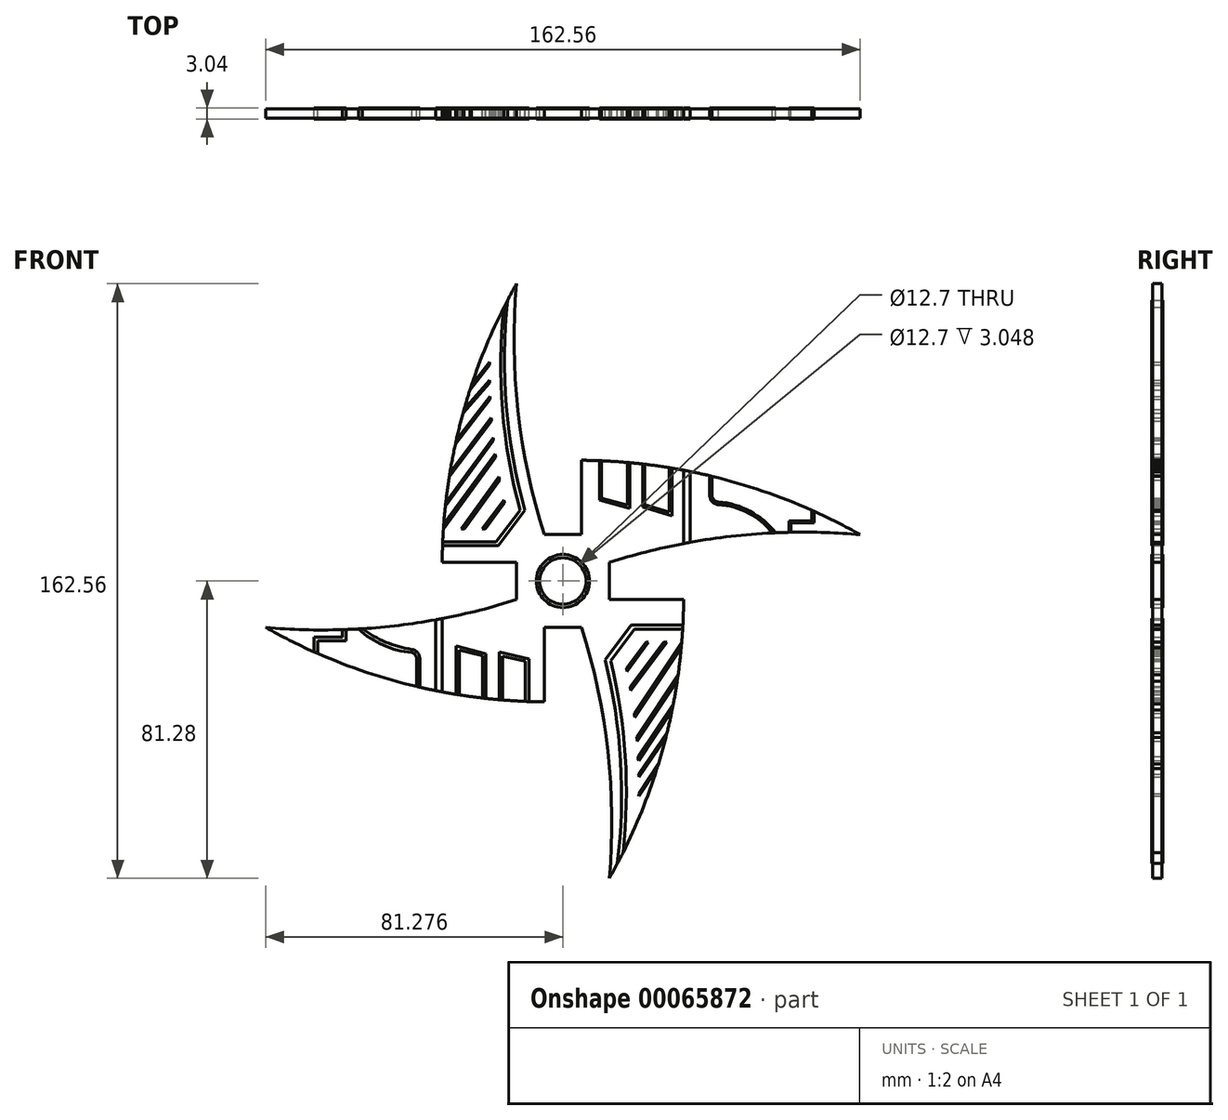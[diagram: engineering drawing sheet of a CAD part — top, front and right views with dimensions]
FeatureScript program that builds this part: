
annotation { "Feature Type Name" : "Feature", "Feature Type Description" : "" }
export const myFeature = defineFeature(function(context is Context, id is Id, definition is map)
    precondition{}
    {
        {
            var Q0;
            Q0=qCreatedBy(makeId("Front.planeOp"),FACE);
            var sketch = newSketch(context, id + "F0", { "sketchPlane" : qUnion([Q0])});
            skCircle(sketch, "E0", {"center": v(-17.65, 17.74) * mm, "radius": 6.35 * mm});
            skLineSegment(sketch, "E1", {"start": v(-22.73, 30.44) * mm, "end": v(-12.57, 30.44) * mm});
            skLineSegment(sketch, "E2", {"start": v(-22.73, 5.04) * mm, "end": v(-12.57, 5.04) * mm});
            skLineSegment(sketch, "E3", {"start": v(-30.35, 22.82) * mm, "end": v(-30.35, 12.66) * mm});
            skLineSegment(sketch, "E4", {"start": v(-4.95, 22.82) * mm, "end": v(-4.95, 12.66) * mm});
            skLineSegment(sketch, "E5", {"start": v(-17.65, 17.74) * mm, "end": v(-17.65, 30.44) * mm, "construction": true});
            skLineSegment(sketch, "E6", {"start": v(-17.65, 17.74) * mm, "end": v(-17.65, 5.04) * mm, "construction": true});
            skLineSegment(sketch, "E7", {"start": v(-17.65, 17.74) * mm, "end": v(-30.35, 17.74) * mm, "construction": true});
            skLineSegment(sketch, "E8", {"start": v(-17.65, 17.74) * mm, "end": v(-4.95, 17.74) * mm, "construction": true});
            skLineSegment(sketch, "E9", {"start": v(-12.57, 30.44) * mm, "end": v(-12.57, 50.76) * mm});
            skLineSegment(sketch, "E10", {"start": v(-4.95, 12.66) * mm, "end": v(15.37, 12.66) * mm});
            skLineSegment(sketch, "E11", {"start": v(-22.73, 5.04) * mm, "end": v(-22.73, -15.28) * mm});
            skLineSegment(sketch, "E12", {"start": v(-30.35, 22.82) * mm, "end": v(-50.67, 22.82) * mm});
            skArc(sketch, "E13", {"start": v(-30.35, 99.02) * mm, "mid": v(-29.96, 64.35) * mm, "end": v(-22.73, 30.44) * mm});
            skArc(sketch, "E14", {"start": v(-30.35, 99.02) * mm, "mid": v(-45.35, 62.21) * mm, "end": v(-50.67, 22.82) * mm});
            skArc(sketch, "E15", {"start": v(63.63, 30.44) * mm, "mid": v(28.96, 30.04) * mm, "end": v(-4.95, 22.82) * mm});
            skArc(sketch, "E16", {"start": v(63.63, 30.44) * mm, "mid": v(26.82, 45.44) * mm, "end": v(-12.57, 50.76) * mm});
            skArc(sketch, "E17", {"start": v(-4.95, -63.54) * mm, "mid": v(-5.35, -28.87) * mm, "end": v(-12.57, 5.04) * mm});
            skArc(sketch, "E18", {"start": v(-4.95, -63.54) * mm, "mid": v(10.05, -26.73) * mm, "end": v(15.37, 12.66) * mm});
            skArc(sketch, "E19", {"start": v(-98.93, 5.04) * mm, "mid": v(-64.26, 5.44) * mm, "end": v(-30.35, 12.66) * mm});
            skArc(sketch, "E20", {"start": v(-98.93, 5.04) * mm, "mid": v(-62.12, -9.96) * mm, "end": v(-22.73, -15.28) * mm});
            skLineSegment(sketch, "E21", {"start": v(-98.93, 5.04) * mm, "end": v(-22.73, 5.04) * mm, "construction": true});
            skLineSegment(sketch, "E22", {"start": v(-30.35, 22.82) * mm, "end": v(-30.35, 99.02) * mm, "construction": true});
            skLineSegment(sketch, "E23", {"start": v(-4.95, -63.54) * mm, "end": v(-4.95, 12.66) * mm, "construction": true});
            skLineSegment(sketch, "E24", {"start": v(-12.57, 30.44) * mm, "end": v(63.63, 30.44) * mm, "construction": true});
            skSolve(sketch);
        }
        {
            var Q0;
            Q0=makeQuery(id+"F0.imprint","IMPRINT",FACE,{"disambiguationData":[TD([[makeQuery(id+"F0.imprint","IMPRINT",EDGE,{"derivedFrom":sQuery(id+"F0.wireOp",EDGE,"E0")}),-1.0]])]});
            extrude(context, id + "F1", {"entities" : qUnion([Q0]), "depth" : 2.54 * mm});
        }
        {
            var Q0;
            Q0=makeQuery(id+"F1.opExtrude","CAP_FACE",FACE,{"disambiguationData":[OSD([sQuery(id+"F0.wireOp",EDGE,"E0"),sQuery(id+"F0.wireOp",EDGE,"E1"),sQuery(id+"F0.wireOp",EDGE,"E2"),sQuery(id+"F0.wireOp",EDGE,"E3"),sQuery(id+"F0.wireOp",EDGE,"E4"),sQuery(id+"F0.wireOp",EDGE,"E9"),sQuery(id+"F0.wireOp",EDGE,"E10"),sQuery(id+"F0.wireOp",EDGE,"E11"),sQuery(id+"F0.wireOp",EDGE,"E12"),sQuery(id+"F0.wireOp",EDGE,"E13"),sQuery(id+"F0.wireOp",EDGE,"E14"),sQuery(id+"F0.wireOp",EDGE,"E15"),sQuery(id+"F0.wireOp",EDGE,"E16"),sQuery(id+"F0.wireOp",EDGE,"E17"),sQuery(id+"F0.wireOp",EDGE,"E18"),sQuery(id+"F0.wireOp",EDGE,"E19"),sQuery(id+"F0.wireOp",EDGE,"E20")])],"isStart":false});
            var sketch = newSketch(context, id + "F2", { "sketchPlane" : qUnion([Q0])});
            skLineSegment(sketch, "E25", {"start": v(-50.53, 28.4) * mm, "end": v(-35.93, 28.4) * mm});
            skArc(sketch, "E26", {"start": v(-33.81, 92.53) * mm, "mid": v(-34.17, 64.62) * mm, "end": v(-29.38, 37.12) * mm});
            skLineSegment(sketch, "E27", {"start": v(-35.93, 28.4) * mm, "end": v(-29.38, 37.12) * mm});
            skArc(sketch, "E28", {"start": v(-37.34, 85.05) * mm, "mid": v(-37.25, 61.92) * mm, "end": v(-33.62, 39.08) * mm});
            skLineSegment(sketch, "E29", {"start": v(-50.33, 32.03) * mm, "end": v(-38.92, 32.03) * mm});
            skLineSegment(sketch, "E30", {"start": v(-38.92, 32.03) * mm, "end": v(-33.62, 39.08) * mm});
            skLineSegment(sketch, "E31", {"start": v(-34.97, 45.3) * mm, "end": v(-44.63, 32.03) * mm});
            skLineSegment(sketch, "E32", {"start": v(-36.06, 51.62) * mm, "end": v(-50.33, 32.03) * mm});
            skLineSegment(sketch, "E33", {"start": v(-36.68, 56.2) * mm, "end": v(-49.8, 38.19) * mm});
            skLineSegment(sketch, "E34", {"start": v(-37.22, 61.53) * mm, "end": v(-48.73, 46.26) * mm});
            skLineSegment(sketch, "E35", {"start": v(-37.6, 67.4) * mm, "end": v(-47.04, 55.25) * mm});
            skLineSegment(sketch, "E36", {"start": v(-37.73, 71.9) * mm, "end": v(-44.98, 63.6) * mm});
            skLineSegment(sketch, "E37", {"start": v(-37.72, 76.84) * mm, "end": v(-43.05, 70.03) * mm});
            skLineSegment(sketch, "E38", {"start": v(-7.06, 50.62) * mm, "end": v(-7.06, 40.35) * mm});
            skLineSegment(sketch, "E39", {"start": v(-7.06, 40.35) * mm, "end": v(0, 38.5) * mm});
            skLineSegment(sketch, "E40", {"start": v(0, 38.5) * mm, "end": v(0, 50.16) * mm});
            skLineSegment(sketch, "E41", {"start": v(4.75, 49.67) * mm, "end": v(4.75, 38.56) * mm});
            skLineSegment(sketch, "E42", {"start": v(4.75, 38.56) * mm, "end": v(11.46, 36.57) * mm});
            skLineSegment(sketch, "E43", {"start": v(11.46, 36.57) * mm, "end": v(11.46, 48.73) * mm});
            skLineSegment(sketch, "E44", {"start": v(15.37, 48.04) * mm, "end": v(15.37, 28) * mm});
            skLineSegment(sketch, "E45", {"start": v(17.18, 28.33) * mm, "end": v(17.18, 47.69) * mm});
            skLineSegment(sketch, "E46", {"start": v(22.5, 46.53) * mm, "end": v(22.5, 41.17) * mm});
            skCircle(sketch, "E47", {"center": v(-17.65, 17.74) * mm, "radius": 7.27 * mm});
            skLineSegment(sketch, "E48", {"start": v(-50.67, 7.49) * mm, "end": v(-50.67, -12.56) * mm});
            skLineSegment(sketch, "E49", {"start": v(-45.94, -13.38) * mm, "end": v(-45.94, -1.07) * mm});
            skLineSegment(sketch, "E50", {"start": v(-45.94, -1.07) * mm, "end": v(-39.58, -2.68) * mm});
            skLineSegment(sketch, "E51", {"start": v(-39.58, -2.68) * mm, "end": v(-39.58, -14.24) * mm});
            skLineSegment(sketch, "E52", {"start": v(-34.2, -14.77) * mm, "end": v(-34.2, -2.78) * mm});
            skLineSegment(sketch, "E53", {"start": v(-34.2, -2.78) * mm, "end": v(-27.89, -4.22) * mm});
            skLineSegment(sketch, "E54", {"start": v(-27.89, -4.22) * mm, "end": v(-27.89, -15.16) * mm});
            skLineSegment(sketch, "E55", {"start": v(-52.49, 7.15) * mm, "end": v(-52.49, -12.2) * mm});
            skLineSegment(sketch, "E56", {"start": v(-56.8, -11.28) * mm, "end": v(-56.8, -3.47) * mm});
            skArc(sketch, "E57", {"start": v(-72.56, 4.71) * mm, "mid": v(-66.1, 1.05) * mm, "end": v(-58.96, -0.96) * mm});
            skPoint(sketch, "E58.visualSharp", {"position": v(-56.8, -1.21) * mm});
            skArc(sketch, "E58.filletArc", {"start": v(-56.8, -3.47) * mm, "mid": v(-57.41, -1.81) * mm, "end": v(-58.96, -0.96) * mm});
            skLineSegment(sketch, "E59", {"start": v(-76.99, 4.49) * mm, "end": v(-76.99, 1.34) * mm});
            skLineSegment(sketch, "E60", {"start": v(-76.99, 1.34) * mm, "end": v(-84.75, 1.34) * mm});
            skLineSegment(sketch, "E61", {"start": v(-84.75, 1.34) * mm, "end": v(-84.75, -2.04) * mm});
            skLineSegment(sketch, "E62", {"start": v(44.22, 31.07) * mm, "end": v(44.22, 34.13) * mm});
            skLineSegment(sketch, "E63", {"start": v(44.22, 34.13) * mm, "end": v(50.44, 34.13) * mm});
            skLineSegment(sketch, "E64", {"start": v(50.44, 34.13) * mm, "end": v(50.44, 37.08) * mm});
            skArc(sketch, "E65", {"start": v(39.59, 30.9) * mm, "mid": v(33.07, 36.35) * mm, "end": v(24.89, 38.64) * mm});
            skPoint(sketch, "E66.visualSharp", {"position": v(22.5, 38.64) * mm});
            skArc(sketch, "E66.filletArc", {"start": v(22.5, 41.17) * mm, "mid": v(23.19, 39.43) * mm, "end": v(24.89, 38.64) * mm});
            skArc(sketch, "E67", {"start": v(-1.2, -56.47) * mm, "mid": v(-0.61, -30.14) * mm, "end": v(-4.62, -4.12) * mm});
            skLineSegment(sketch, "E68", {"start": v(-4.62, -4.12) * mm, "end": v(1.9, 4.56) * mm});
            skLineSegment(sketch, "E69", {"start": v(1.9, 4.56) * mm, "end": v(15.1, 4.56) * mm});
            skLineSegment(sketch, "E70", {"start": v(5.02, 1) * mm, "end": v(14.84, 1) * mm});
            skLineSegment(sketch, "E71", {"start": v(5.02, 1) * mm, "end": v(-0.28, -6.04) * mm});
            skArc(sketch, "E72", {"start": v(2.82, -47.75) * mm, "mid": v(2.72, -26.79) * mm, "end": v(-0.28, -6.04) * mm});
            skLineSegment(sketch, "E73", {"start": v(0.75, -11.2) * mm, "end": v(9.93, 1) * mm});
            skLineSegment(sketch, "E74", {"start": v(1.87, -18.44) * mm, "end": v(14.84, 1) * mm});
            skLineSegment(sketch, "E75", {"start": v(2.57, -24.84) * mm, "end": v(13.85, -7.92) * mm});
            skLineSegment(sketch, "E76", {"start": v(2.94, -30.25) * mm, "end": v(12.53, -15.88) * mm});
            skLineSegment(sketch, "E77", {"start": v(3.12, -40.32) * mm, "end": v(8.46, -32.26) * mm});
            skLineSegment(sketch, "E78", {"start": v(3.11, -35.02) * mm, "end": v(10.82, -23.73) * mm});
            skLineSegment(sketch, "E79", {"start": v(-37.7, 77.6) * mm, "end": v(-42.64, 71.29) * mm});
            skLineSegment(sketch, "E80", {"start": v(-37.74, 72.63) * mm, "end": v(-44.67, 64.68) * mm});
            skLineSegment(sketch, "E81", {"start": v(-37.63, 68.2) * mm, "end": v(-46.78, 56.44) * mm});
            skLineSegment(sketch, "E82", {"start": v(-37.29, 62.36) * mm, "end": v(-48.54, 47.44) * mm});
            skLineSegment(sketch, "E83", {"start": v(-36.76, 56.94) * mm, "end": v(-49.7, 39.19) * mm});
            skLineSegment(sketch, "E84", {"start": v(-36.2, 52.52) * mm, "end": v(-50.25, 33.22) * mm});
            skLineSegment(sketch, "E85", {"start": v(-35.14, 46.2) * mm, "end": v(-45.47, 32.03) * mm});
            skLineSegment(sketch, "E86", {"start": v(-33.8, 39.85) * mm, "end": v(-39.7, 32.03) * mm});
            skLineSegment(sketch, "E87", {"start": v(-50.57, 27.5) * mm, "end": v(-35.27, 27.5) * mm});
            skLineSegment(sketch, "E88", {"start": v(-35.27, 27.5) * mm, "end": v(-28.03, 37.12) * mm});
            skLineSegment(sketch, "E89", {"start": v(-7.65, 50.64) * mm, "end": v(-7.65, 39.9) * mm});
            skLineSegment(sketch, "E90", {"start": v(-7.65, 39.9) * mm, "end": v(0.6, 37.66) * mm});
            skLineSegment(sketch, "E91", {"start": v(0.6, 37.66) * mm, "end": v(0.6, 50.1) * mm});
            skLineSegment(sketch, "E92", {"start": v(4.14, 49.74) * mm, "end": v(4.14, 37.98) * mm});
            skLineSegment(sketch, "E93", {"start": v(4.14, 37.98) * mm, "end": v(12.13, 35.61) * mm});
            skLineSegment(sketch, "E94", {"start": v(12.13, 35.61) * mm, "end": v(12.13, 48.61) * mm});
            skLineSegment(sketch, "E95", {"start": v(23.15, 46.37) * mm, "end": v(23.15, 41.17) * mm});
            skLineSegment(sketch, "E96", {"start": v(44.7, 31.08) * mm, "end": v(44.7, 33.62) * mm});
            skLineSegment(sketch, "E97", {"start": v(44.7, 33.62) * mm, "end": v(51, 33.62) * mm});
            skLineSegment(sketch, "E98", {"start": v(51, 33.62) * mm, "end": v(51, 36.83) * mm});
            skArc(sketch, "E99", {"start": v(40.46, 30.94) * mm, "mid": v(33.56, 36.8) * mm, "end": v(24.89, 39.36) * mm});
            skArc(sketch, "E100", {"start": v(23.15, 41.17) * mm, "mid": v(23.65, 39.92) * mm, "end": v(24.89, 39.36) * mm});
            skArc(sketch, "E101", {"start": v(-32.81, 94.49) * mm, "mid": v(-33.09, 65.58) * mm, "end": v(-28.03, 37.12) * mm});
            skLineSegment(sketch, "E102", {"start": v(-85.76, -1.6) * mm, "end": v(-85.76, 2.4) * mm});
            skLineSegment(sketch, "E103", {"start": v(-85.76, 2.4) * mm, "end": v(-77.92, 2.4) * mm});
            skLineSegment(sketch, "E104", {"start": v(-77.92, 2.4) * mm, "end": v(-77.92, 4.46) * mm});
            skLineSegment(sketch, "E105", {"start": v(-57.65, -11.08) * mm, "end": v(-57.65, -3.63) * mm});
            skArc(sketch, "E106", {"start": v(-73.58, 4.65) * mm, "mid": v(-66.8, 0.22) * mm, "end": v(-58.96, -1.8) * mm});
            skArc(sketch, "E107", {"start": v(-57.65, -3.63) * mm, "mid": v(-58.01, -2.5) * mm, "end": v(-58.96, -1.8) * mm});
            skLineSegment(sketch, "E108", {"start": v(-46.9, -13.23) * mm, "end": v(-46.9, -0.02) * mm});
            skLineSegment(sketch, "E109", {"start": v(-46.9, -0.02) * mm, "end": v(-38.68, -2.15) * mm});
            skLineSegment(sketch, "E110", {"start": v(-38.68, -2.15) * mm, "end": v(-38.68, -14.35) * mm});
            skLineSegment(sketch, "E111", {"start": v(-35.08, -14.7) * mm, "end": v(-35.08, -1.65) * mm});
            skLineSegment(sketch, "E112", {"start": v(-26.98, -15.19) * mm, "end": v(-26.98, -3.53) * mm});
            skLineSegment(sketch, "E113", {"start": v(-26.98, -3.53) * mm, "end": v(-35.08, -1.65) * mm});
            skCircle(sketch, "E114", {"center": v(-17.65, 17.74) * mm, "radius": 6.35 * mm});
            skLineSegment(sketch, "E115", {"start": v(15.16, 5.68) * mm, "end": v(1.01, 5.68) * mm});
            skLineSegment(sketch, "E116", {"start": v(1.01, 5.68) * mm, "end": v(-6.07, -3.76) * mm});
            skLineSegment(sketch, "E117", {"start": v(5.75, 1) * mm, "end": v(-0.08, -6.97) * mm});
            skLineSegment(sketch, "E118", {"start": v(0.9, -12.12) * mm, "end": v(10.84, 1) * mm});
            skLineSegment(sketch, "E119", {"start": v(2, -19.5) * mm, "end": v(14.72, -0.46) * mm});
            skLineSegment(sketch, "E120", {"start": v(2.67, -26.02) * mm, "end": v(13.6, -9.62) * mm});
            skLineSegment(sketch, "E121", {"start": v(3, -31.36) * mm, "end": v(12.2, -17.56) * mm});
            skLineSegment(sketch, "E122", {"start": v(3.12, -35.83) * mm, "end": v(10.49, -25.03) * mm});
            skLineSegment(sketch, "E123", {"start": v(3.1, -41.02) * mm, "end": v(8.07, -33.54) * mm});
            skArc(sketch, "E124", {"start": v(-2.73, -59.47) * mm, "mid": v(-1.89, -31.46) * mm, "end": v(-6.07, -3.76) * mm});
            skLineSegment(sketch, "E125", {"start": v(-50.38, 31.19) * mm, "end": v(-38.54, 31.19) * mm});
            skLineSegment(sketch, "E126", {"start": v(-38.54, 31.19) * mm, "end": v(-32.72, 38.92) * mm});
            skArc(sketch, "E127", {"start": v(-36.53, 86.87) * mm, "mid": v(-36.38, 62.75) * mm, "end": v(-32.72, 38.92) * mm});
            skArc(sketch, "E128", {"start": v(2.23, -49.13) * mm, "mid": v(1.93, -27.22) * mm, "end": v(-1.08, -5.51) * mm});
            skLineSegment(sketch, "E129", {"start": v(-1.08, -5.51) * mm, "end": v(4.67, 2.07) * mm});
            skLineSegment(sketch, "E130", {"start": v(4.67, 2.07) * mm, "end": v(14.93, 2.07) * mm});
            skArc(sketch, "E131", {"start": v(-30.35, 99.02) * mm, "mid": v(-45.35, 62.21) * mm, "end": v(-50.67, 22.82) * mm});
            skArc(sketch, "E132", {"start": v(63.63, 30.44) * mm, "mid": v(26.82, 45.44) * mm, "end": v(-12.57, 50.76) * mm});
            skArc(sketch, "E133", {"start": v(-4.95, -63.54) * mm, "mid": v(10.05, -26.73) * mm, "end": v(15.37, 12.66) * mm});
            skArc(sketch, "E134", {"start": v(-98.93, 5.04) * mm, "mid": v(-62.12, -9.96) * mm, "end": v(-22.73, -15.28) * mm});
            skArc(sketch, "E135", {"start": v(-98.93, 5.04) * mm, "mid": v(-64.26, 5.44) * mm, "end": v(-30.35, 12.66) * mm});
            skArc(sketch, "E136", {"start": v(-30.35, 99.02) * mm, "mid": v(-29.96, 64.35) * mm, "end": v(-22.73, 30.44) * mm});
            skArc(sketch, "E137", {"start": v(63.63, 30.44) * mm, "mid": v(28.96, 30.04) * mm, "end": v(-4.95, 22.82) * mm});
            skArc(sketch, "E138", {"start": v(-12.57, 5.04) * mm, "mid": v(-5.35, -28.87) * mm, "end": v(-4.95, -63.54) * mm});
            skLineSegment(sketch, "E139", {"start": v(-22.73, -15.28) * mm, "end": v(-22.73, 5.04) * mm});
            skLineSegment(sketch, "E140", {"start": v(-22.73, 5.04) * mm, "end": v(-12.57, 5.04) * mm});
            skLineSegment(sketch, "E141", {"start": v(-30.35, 12.66) * mm, "end": v(-30.35, 22.82) * mm});
            skLineSegment(sketch, "E142", {"start": v(-50.67, 22.82) * mm, "end": v(-30.35, 22.82) * mm});
            skLineSegment(sketch, "E143", {"start": v(-22.73, 30.44) * mm, "end": v(-12.57, 30.44) * mm});
            skLineSegment(sketch, "E144", {"start": v(-12.57, 30.44) * mm, "end": v(-12.57, 50.76) * mm});
            skLineSegment(sketch, "E145", {"start": v(-4.95, 22.82) * mm, "end": v(-4.95, 12.66) * mm});
            skLineSegment(sketch, "E146", {"start": v(-4.95, 12.66) * mm, "end": v(15.37, 12.66) * mm});
            skSolve(sketch);
        }
        {
            var Q0;
            {var subQ2=sQuery(id+"F2.wireOp",EDGE,"E25");Q0=makeQuery(id+"F2.imprint","IMPRINT",FACE,{"disambiguationData":[TD([[makeQuery(id+"F2.imprint","IMPRINT",EDGE,{"derivedFrom":subQ2}),-1.0]])]});}
            var Q1;
            {var subQ0=sQuery(id+"F2.wireOp",EDGE,"E30");Q1=makeQuery(id+"F2.imprint","IMPRINT",FACE,{"disambiguationData":[TD([[makeQuery(id+"F2.imprint","IMPRINT",EDGE,{"derivedFrom":subQ0}),1.0]])]});}
            var Q2;
            {var subQ0=sQuery(id+"F2.wireOp",EDGE,"E31");Q2=makeQuery(id+"F2.imprint","IMPRINT",FACE,{"disambiguationData":[TD([[makeQuery(id+"F2.imprint","IMPRINT",EDGE,{"derivedFrom":subQ0}),-1.0]])]});}
            var Q3;
            {var subQ0=sQuery(id+"F2.wireOp",EDGE,"E32");Q3=makeQuery(id+"F2.imprint","IMPRINT",FACE,{"disambiguationData":[TD([[makeQuery(id+"F2.imprint","IMPRINT",EDGE,{"derivedFrom":subQ0}),-1.0]])]});}
            var Q4;
            {var subQ0=sQuery(id+"F2.wireOp",EDGE,"E33");Q4=makeQuery(id+"F2.imprint","IMPRINT",FACE,{"disambiguationData":[TD([[makeQuery(id+"F2.imprint","IMPRINT",EDGE,{"derivedFrom":subQ0}),-1.0]])]});}
            var Q5;
            {var subQ0=sQuery(id+"F2.wireOp",EDGE,"E34");Q5=makeQuery(id+"F2.imprint","IMPRINT",FACE,{"disambiguationData":[TD([[makeQuery(id+"F2.imprint","IMPRINT",EDGE,{"derivedFrom":subQ0}),-1.0]])]});}
            var Q6;
            {var subQ0=sQuery(id+"F2.wireOp",EDGE,"E35");Q6=makeQuery(id+"F2.imprint","IMPRINT",FACE,{"disambiguationData":[TD([[makeQuery(id+"F2.imprint","IMPRINT",EDGE,{"derivedFrom":subQ0}),-1.0]])]});}
            var Q7;
            {var subQ0=sQuery(id+"F2.wireOp",EDGE,"E36");Q7=makeQuery(id+"F2.imprint","IMPRINT",FACE,{"disambiguationData":[TD([[makeQuery(id+"F2.imprint","IMPRINT",EDGE,{"derivedFrom":subQ0}),-1.0]])]});}
            var Q8;
            {var subQ0=sQuery(id+"F2.wireOp",EDGE,"E37");Q8=makeQuery(id+"F2.imprint","IMPRINT",FACE,{"disambiguationData":[TD([[makeQuery(id+"F2.imprint","IMPRINT",EDGE,{"derivedFrom":subQ0}),-1.0]])]});}
            var Q9;
            {var subQ2=sQuery(id+"F2.wireOp",EDGE,"E38");Q9=makeQuery(id+"F2.imprint","IMPRINT",FACE,{"disambiguationData":[TD([[makeQuery(id+"F2.imprint","IMPRINT",EDGE,{"derivedFrom":subQ2}),-1.0]])]});}
            var Q10;
            {var subQ2=sQuery(id+"F2.wireOp",EDGE,"E41");Q10=makeQuery(id+"F2.imprint","IMPRINT",FACE,{"disambiguationData":[TD([[makeQuery(id+"F2.imprint","IMPRINT",EDGE,{"derivedFrom":subQ2}),-1.0]])]});}
            var Q11;
            {var subQ0=sQuery(id+"F2.wireOp",EDGE,"E44");Q11=makeQuery(id+"F2.imprint","IMPRINT",FACE,{"disambiguationData":[TD([[makeQuery(id+"F2.imprint","IMPRINT",EDGE,{"derivedFrom":subQ0}),1.0]])]});}
            var Q12;
            {var subQ2=sQuery(id+"F2.wireOp",EDGE,"E46");Q12=makeQuery(id+"F2.imprint","IMPRINT",FACE,{"disambiguationData":[TD([[makeQuery(id+"F2.imprint","IMPRINT",EDGE,{"derivedFrom":subQ2}),1.0]])]});}
            var Q13;
            {var subQ1=sQuery(id+"F2.wireOp",EDGE,"E62");Q13=makeQuery(id+"F2.imprint","IMPRINT",FACE,{"disambiguationData":[TD([[makeQuery(id+"F2.imprint","IMPRINT",EDGE,{"derivedFrom":subQ1}),-1.0]])]});}
            var Q14;
            Q14=makeQuery(id+"F2.imprint","IMPRINT",FACE,{"disambiguationData":[TD([[makeQuery(id+"F2.imprint","IMPRINT",EDGE,{"derivedFrom":sQuery(id+"F2.wireOp",EDGE,"E47")}),1.0]])]});
            var Q15;
            {var subQ2=sQuery(id+"F2.wireOp",EDGE,"E52");Q15=makeQuery(id+"F2.imprint","IMPRINT",FACE,{"disambiguationData":[TD([[makeQuery(id+"F2.imprint","IMPRINT",EDGE,{"derivedFrom":subQ2}),1.0]])]});}
            var Q16;
            {var subQ2=sQuery(id+"F2.wireOp",EDGE,"E49");Q16=makeQuery(id+"F2.imprint","IMPRINT",FACE,{"disambiguationData":[TD([[makeQuery(id+"F2.imprint","IMPRINT",EDGE,{"derivedFrom":subQ2}),1.0]])]});}
            var Q17;
            {var subQ0=sQuery(id+"F2.wireOp",EDGE,"E48");Q17=makeQuery(id+"F2.imprint","IMPRINT",FACE,{"disambiguationData":[TD([[makeQuery(id+"F2.imprint","IMPRINT",EDGE,{"derivedFrom":subQ0}),-1.0]])]});}
            var Q18;
            {var subQ4=sQuery(id+"F2.wireOp",EDGE,"E56");Q18=makeQuery(id+"F2.imprint","IMPRINT",FACE,{"disambiguationData":[TD([[makeQuery(id+"F2.imprint","IMPRINT",EDGE,{"derivedFrom":subQ4}),1.0]])]});}
            var Q19;
            {var subQ2=sQuery(id+"F2.wireOp",EDGE,"E59");Q19=makeQuery(id+"F2.imprint","IMPRINT",FACE,{"disambiguationData":[TD([[makeQuery(id+"F2.imprint","IMPRINT",EDGE,{"derivedFrom":subQ2}),-1.0]])]});}
            var Q20;
            {var subQ3=sQuery(id+"F2.wireOp",EDGE,"E67");Q20=makeQuery(id+"F2.imprint","IMPRINT",FACE,{"disambiguationData":[TD([[makeQuery(id+"F2.imprint","IMPRINT",EDGE,{"derivedFrom":subQ3}),1.0]])]});}
            var Q21;
            {var subQ0=sQuery(id+"F2.wireOp",EDGE,"E71");Q21=makeQuery(id+"F2.imprint","IMPRINT",FACE,{"disambiguationData":[TD([[makeQuery(id+"F2.imprint","IMPRINT",EDGE,{"derivedFrom":subQ0}),1.0]])]});}
            var Q22;
            {var subQ0=sQuery(id+"F2.wireOp",EDGE,"E73");Q22=makeQuery(id+"F2.imprint","IMPRINT",FACE,{"disambiguationData":[TD([[makeQuery(id+"F2.imprint","IMPRINT",EDGE,{"derivedFrom":subQ0}),-1.0]])]});}
            var Q23;
            {var subQ0=sQuery(id+"F2.wireOp",EDGE,"E74");Q23=makeQuery(id+"F2.imprint","IMPRINT",FACE,{"disambiguationData":[TD([[makeQuery(id+"F2.imprint","IMPRINT",EDGE,{"derivedFrom":subQ0}),-1.0]])]});}
            var Q24;
            {var subQ0=sQuery(id+"F2.wireOp",EDGE,"E75");Q24=makeQuery(id+"F2.imprint","IMPRINT",FACE,{"disambiguationData":[TD([[makeQuery(id+"F2.imprint","IMPRINT",EDGE,{"derivedFrom":subQ0}),-1.0]])]});}
            var Q25;
            {var subQ0=sQuery(id+"F2.wireOp",EDGE,"E76");Q25=makeQuery(id+"F2.imprint","IMPRINT",FACE,{"disambiguationData":[TD([[makeQuery(id+"F2.imprint","IMPRINT",EDGE,{"derivedFrom":subQ0}),-1.0]])]});}
            var Q26;
            {var subQ0=sQuery(id+"F2.wireOp",EDGE,"E78");Q26=makeQuery(id+"F2.imprint","IMPRINT",FACE,{"disambiguationData":[TD([[makeQuery(id+"F2.imprint","IMPRINT",EDGE,{"derivedFrom":subQ0}),-1.0]])]});}
            var Q27;
            {var subQ0=sQuery(id+"F2.wireOp",EDGE,"E77");Q27=makeQuery(id+"F2.imprint","IMPRINT",FACE,{"disambiguationData":[TD([[makeQuery(id+"F2.imprint","IMPRINT",EDGE,{"derivedFrom":subQ0}),-1.0]])]});}
            extrude(context, id + "F3", {"entities" : qUnion([Q0, Q1, Q2, Q3, Q4, Q5, Q6, Q7, Q8, Q9, Q10, Q11, Q12, Q13, Q14, Q15, Q16, Q17, Q18, Q19, Q20, Q21, Q22, Q23, Q24, Q25, Q26, Q27]), "depth" : 0.25 * mm, "hasSecondDirection" : true, "secondDirectionOppositeDirection" : true, "secondDirectionDepth" : 2.8 * mm});
        }
    });
